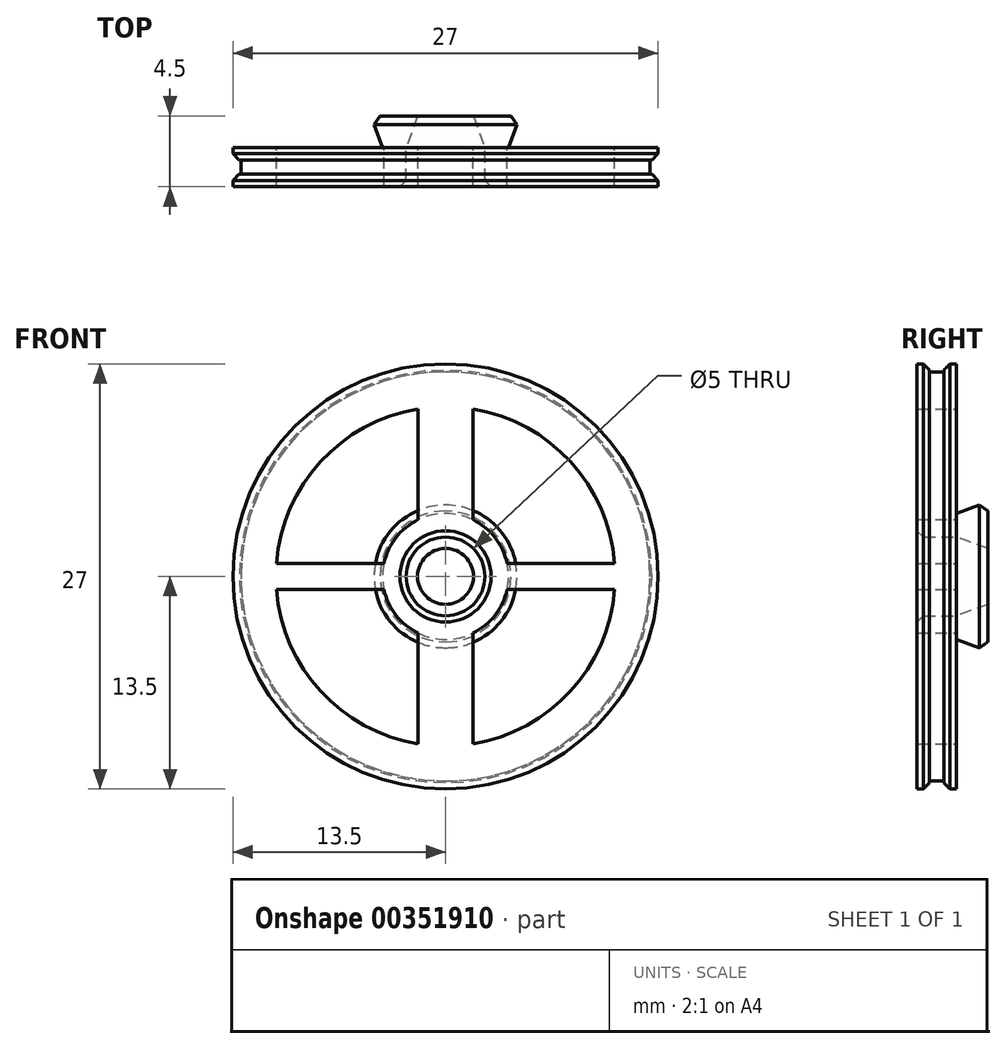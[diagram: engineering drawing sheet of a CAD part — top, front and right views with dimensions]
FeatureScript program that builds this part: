
annotation { "Feature Type Name" : "Feature", "Feature Type Description" : "" }
export const myFeature = defineFeature(function(context is Context, id is Id, definition is map)
    precondition{}
    {
        {
            var Q0;
            Q0=qCreatedBy(makeId("Front.planeOp"),FACE);
            var sketch = newSketch(context, id + "F0", { "sketchPlane" : qUnion([Q0])});
            skCircle(sketch, "E0", {"center": v(0, 0) * mm, "radius": 13 * mm});
            skArc(sketch, "E1", {"start": v(-10.74, -0.83) * mm, "mid": v(-7.94, -7.29) * mm, "end": v(-1.74, -10.63) * mm});
            skLineSegment(sketch, "E2.bottom", {"start": v(10.74, 0.83) * mm, "end": v(3.91, 0.83) * mm});
            skLineSegment(sketch, "E2.top", {"start": v(10.74, -0.83) * mm, "end": v(3.91, -0.83) * mm});
            skLineSegment(sketch, "E3.left", {"start": v(0.69, 10.75) * mm, "end": v(0.69, 10.75) * mm});
            skArc(sketch, "E4", {"start": v(-3.91, -0.83) * mm, "mid": v(-3.15, -2.47) * mm, "end": v(-1.74, -3.6) * mm});
            skLineSegment(sketch, "E5.trimOffspring", {"start": v(-3.91, 0.83) * mm, "end": v(-10.74, 0.83) * mm});
            skLineSegment(sketch, "E6.trimOffspring", {"start": v(-3.91, -0.83) * mm, "end": v(-10.74, -0.83) * mm});
            skArc(sketch, "E7.trimOffspring", {"start": v(-1.74, 3.6) * mm, "mid": v(-3.15, 2.47) * mm, "end": v(-3.91, 0.83) * mm});
            skArc(sketch, "E8.trimOffspring", {"start": v(3.91, 0.83) * mm, "mid": v(3.15, 2.47) * mm, "end": v(1.74, 3.6) * mm});
            skArc(sketch, "E9.trimOffspring", {"start": v(1.74, -3.6) * mm, "mid": v(3.15, -2.47) * mm, "end": v(3.91, -0.83) * mm});
            skCircle(sketch, "E10", {"center": v(0, 0) * mm, "radius": 2.5 * mm});
            skArc(sketch, "E11.trimOffspring", {"start": v(-1.74, 10.63) * mm, "mid": v(-7.94, 7.29) * mm, "end": v(-10.74, 0.83) * mm});
            skArc(sketch, "E12.trimOffspring", {"start": v(10.74, 0.83) * mm, "mid": v(7.94, 7.29) * mm, "end": v(1.74, 10.63) * mm});
            skArc(sketch, "E13.trimOffspring", {"start": v(1.74, -10.63) * mm, "mid": v(7.94, -7.29) * mm, "end": v(10.74, -0.83) * mm});
            skLineSegment(sketch, "E14.right", {"start": v(-1.74, 10.63) * mm, "end": v(-1.74, 3.6) * mm});
            skLineSegment(sketch, "E15.trimOffspring", {"start": v(-1.74, -3.6) * mm, "end": v(-1.74, -10.63) * mm});
            skLineSegment(sketch, "E16.trimOffspring", {"start": v(1.74, -3.6) * mm, "end": v(1.74, -10.63) * mm});
            skLineSegment(sketch, "E17", {"start": v(1.74, 3.6) * mm, "end": v(1.74, 10.63) * mm});
            skPoint(sketch, "E18.trimOffspring.end.orphan", {"position": v(0.69, -10.75) * mm});
            skPoint(sketch, "E19.trimOffspring.end.orphan", {"position": v(-0.69, -10.75) * mm});
            skPoint(sketch, "E3.right.start.orphan", {"position": v(-0.69, 10.75) * mm});
            skSolve(sketch);
        }
        {
            var Q0;
            Q0 = qSketchRegion(id + "F0", true);
            extrude(context, id + "F1", {"entities" : qUnion([Q0]), "depth" : 2.5 * mm});
        }
        {
            var Q0;
            Q0=makeQuery(id+"F1.opExtrude","CAP_FACE",FACE,{"disambiguationData":[OSD([sQuery(id+"F0.wireOp",EDGE,"E0"),sQuery(id+"F0.wireOp",EDGE,"E1"),sQuery(id+"F0.wireOp",EDGE,"E2.bottom"),sQuery(id+"F0.wireOp",EDGE,"E2.top"),sQuery(id+"F0.wireOp",EDGE,"E4"),sQuery(id+"F0.wireOp",EDGE,"E5.trimOffspring"),sQuery(id+"F0.wireOp",EDGE,"E6.trimOffspring"),sQuery(id+"F0.wireOp",EDGE,"E7.trimOffspring"),sQuery(id+"F0.wireOp",EDGE,"E8.trimOffspring"),sQuery(id+"F0.wireOp",EDGE,"E9.trimOffspring"),sQuery(id+"F0.wireOp",EDGE,"E10"),sQuery(id+"F0.wireOp",EDGE,"E11.trimOffspring"),sQuery(id+"F0.wireOp",EDGE,"E12.trimOffspring"),sQuery(id+"F0.wireOp",EDGE,"E13.trimOffspring"),sQuery(id+"F0.wireOp",EDGE,"E14.right"),sQuery(id+"F0.wireOp",EDGE,"E15.trimOffspring"),sQuery(id+"F0.wireOp",EDGE,"E16.trimOffspring"),sQuery(id+"F0.wireOp",EDGE,"E17")])],"isStart":true});
            var sketch = newSketch(context, id + "F2", { "sketchPlane" : qUnion([Q0])});
            skCircle(sketch, "E20", {"center": v(0, 0) * mm, "radius": 10.9 * mm});
            skCircle(sketch, "E21", {"center": v(0, 0) * mm, "radius": 13.5 * mm});
            skSolve(sketch);
        }
        {
            var Q0;
            Q0 = qSketchRegion(id + "F2", true);
            extrude(context, id + "F3", {"entities" : qUnion([Q0]), "operationType" : NewBodyOperationType.ADD, "oppositeDirection" : true, "depth" : .8 * mm});
        }
        {
            var Q0;
            Q0=makeQuery(id+"F1.opExtrude","CAP_FACE",FACE,{"disambiguationData":[OSD([sQuery(id+"F0.wireOp",EDGE,"E0"),sQuery(id+"F0.wireOp",EDGE,"E1"),sQuery(id+"F0.wireOp",EDGE,"E2.bottom"),sQuery(id+"F0.wireOp",EDGE,"E2.top"),sQuery(id+"F0.wireOp",EDGE,"E4"),sQuery(id+"F0.wireOp",EDGE,"E5.trimOffspring"),sQuery(id+"F0.wireOp",EDGE,"E6.trimOffspring"),sQuery(id+"F0.wireOp",EDGE,"E7.trimOffspring"),sQuery(id+"F0.wireOp",EDGE,"E8.trimOffspring"),sQuery(id+"F0.wireOp",EDGE,"E9.trimOffspring"),sQuery(id+"F0.wireOp",EDGE,"E10"),sQuery(id+"F0.wireOp",EDGE,"E11.trimOffspring"),sQuery(id+"F0.wireOp",EDGE,"E12.trimOffspring"),sQuery(id+"F0.wireOp",EDGE,"E13.trimOffspring"),sQuery(id+"F0.wireOp",EDGE,"E14.right"),sQuery(id+"F0.wireOp",EDGE,"E15.trimOffspring"),sQuery(id+"F0.wireOp",EDGE,"E16.trimOffspring"),sQuery(id+"F0.wireOp",EDGE,"E17")])],"isStart":false});
            var sketch = newSketch(context, id + "F4", { "sketchPlane" : qUnion([Q0])});
            skCircle(sketch, "E22", {"center": v(0, 0) * mm, "radius": 11.25 * mm});
            skCircle(sketch, "E23", {"center": v(0, 0) * mm, "radius": 13.5 * mm});
            skSolve(sketch);
        }
        {
            var Q0;
            Q0 = qSketchRegion(id + "F4", true);
            extrude(context, id + "F5", {"entities" : qUnion([Q0]), "operationType" : NewBodyOperationType.ADD, "oppositeDirection" : true, "depth" : .8 * mm});
        }
        {
            var Q0;
            Q0=makeQuery(id+"F3.boolean.opBoolean","MERGE",FACE,{"derivedFrom":[makeQuery(id+"F1.opExtrude","CAP_FACE",FACE,{"disambiguationData":[OSD([sQuery(id+"F0.wireOp",EDGE,"E0"),sQuery(id+"F0.wireOp",EDGE,"E1"),sQuery(id+"F0.wireOp",EDGE,"E2.bottom"),sQuery(id+"F0.wireOp",EDGE,"E2.top"),sQuery(id+"F0.wireOp",EDGE,"E4"),sQuery(id+"F0.wireOp",EDGE,"E5.trimOffspring"),sQuery(id+"F0.wireOp",EDGE,"E6.trimOffspring"),sQuery(id+"F0.wireOp",EDGE,"E7.trimOffspring"),sQuery(id+"F0.wireOp",EDGE,"E8.trimOffspring"),sQuery(id+"F0.wireOp",EDGE,"E9.trimOffspring"),sQuery(id+"F0.wireOp",EDGE,"E10"),sQuery(id+"F0.wireOp",EDGE,"E11.trimOffspring"),sQuery(id+"F0.wireOp",EDGE,"E12.trimOffspring"),sQuery(id+"F0.wireOp",EDGE,"E13.trimOffspring"),sQuery(id+"F0.wireOp",EDGE,"E14.right"),sQuery(id+"F0.wireOp",EDGE,"E15.trimOffspring"),sQuery(id+"F0.wireOp",EDGE,"E16.trimOffspring"),sQuery(id+"F0.wireOp",EDGE,"E17")])],"isStart":true}),makeQuery(id+"F3.opExtrude","CAP_FACE",FACE,{"disambiguationData":[OSD([sQuery(id+"F2.wireOp",EDGE,"E20"),sQuery(id+"F2.wireOp",EDGE,"E21")])],"isStart":true})]});
            var sketch = newSketch(context, id + "F6", { "sketchPlane" : qUnion([Q0])});
            skCircle(sketch, "E24", {"center": v(0, 0) * mm, "radius": 2.5 * mm});
            skCircle(sketch, "E25", {"center": v(0, 0) * mm, "radius": 4 * mm});
            skSolve(sketch);
        }
        {
            var Q0;
            Q0 = qSketchRegion(id + "F6", true);
            extrude(context, id + "F7", {"entities" : qUnion([Q0]), "operationType" : NewBodyOperationType.ADD, "depth" : 2 * mm, "hasDraft" : true, "draftAngle" : 20 * degree});
        }
        {
            var Q0;
            Q0=makeQuery(id+"F5.opExtrude","CAP_EDGE",EDGE,{"disambiguationData":[OSD([sQuery(id+"F4.wireOp",EDGE,"E23")])],"isStart":false});
            var Q1;
            Q1=makeQuery(id+"F3.opExtrude","CAP_EDGE",EDGE,{"disambiguationData":[OSD([sQuery(id+"F2.wireOp",EDGE,"E21")])],"isStart":false});
            var Q2;
            Q2=makeQuery(id+"F1.opExtrude","CAP_EDGE",EDGE,{"disambiguationData":[OSD([sQuery(id+"F0.wireOp",EDGE,"E10")])],"isStart":false});
            var Q3;
            Q3=makeQuery(id+"F7.opExtrude","CAP_EDGE",EDGE,{"disambiguationData":[OSD([sQuery(id+"F6.wireOp",EDGE,"E25")])],"isStart":false});
            chamfer(context, id + "F8", {"entities" : qUnion([Q0, Q1, Q2, Q3]), "width" : .4 * mm, "tangentPropagation" : true});
        }
    });
